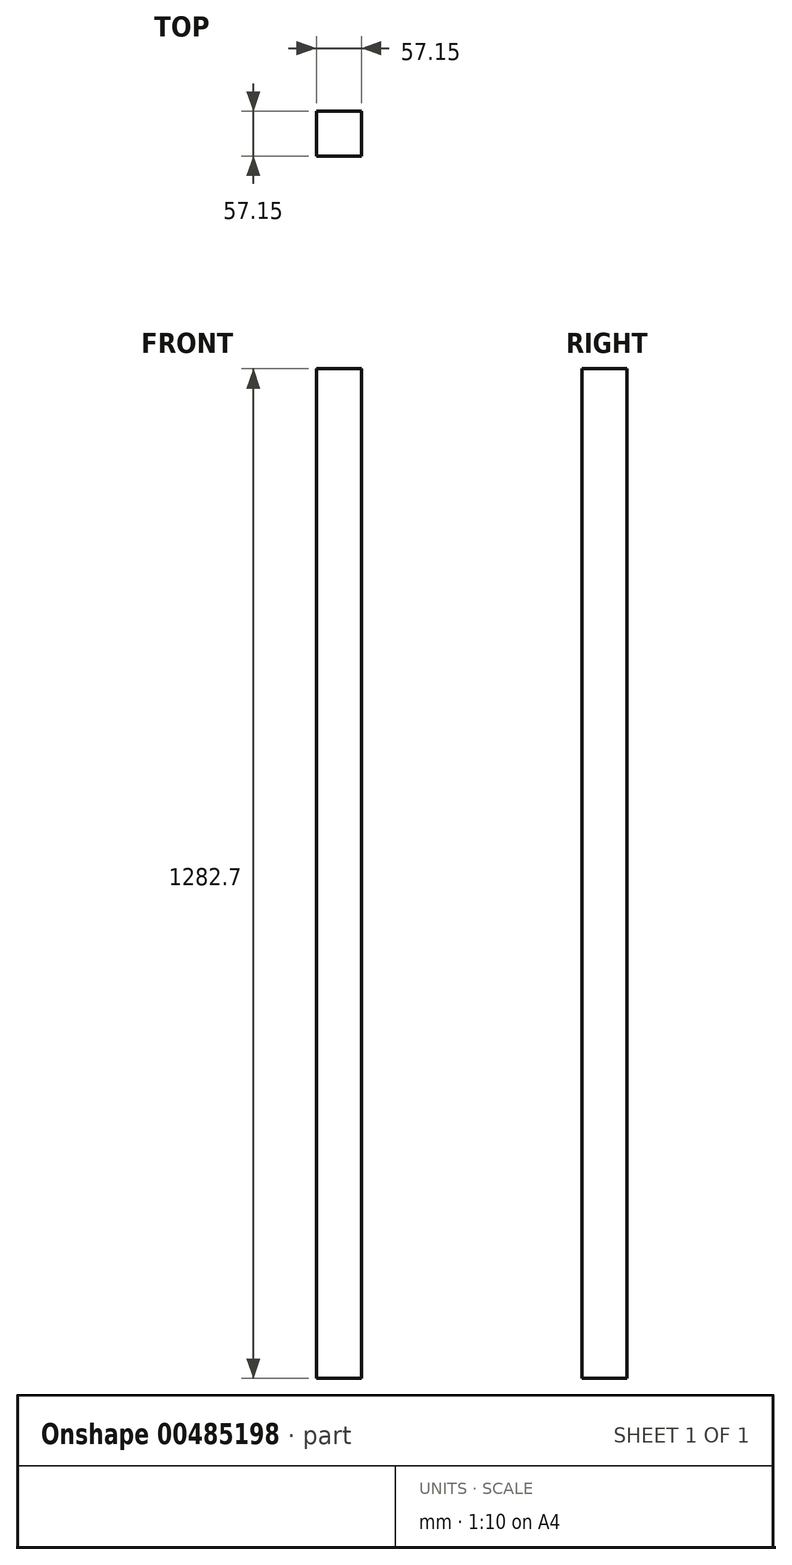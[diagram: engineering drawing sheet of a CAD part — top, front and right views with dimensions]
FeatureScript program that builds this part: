
annotation { "Feature Type Name" : "Feature", "Feature Type Description" : "" }
export const myFeature = defineFeature(function(context is Context, id is Id, definition is map)
    precondition{}
    {
        {
            var Q0;
            Q0=qCreatedBy(makeId("Front.planeOp"),FACE);
            var sketch = newSketch(context, id + "F0", { "sketchPlane" : qUnion([Q0])});
            skLineSegment(sketch, "E0.bottom", {"start": v(0, 0) * mm, "end": v(57.15, 0) * mm});
            skLineSegment(sketch, "E0.top", {"start": v(0, -1282.7) * mm, "end": v(57.15, -1282.7) * mm});
            skLineSegment(sketch, "E0.left", {"start": v(0, 0) * mm, "end": v(0, -1282.7) * mm});
            skLineSegment(sketch, "E0.right", {"start": v(57.15, 0) * mm, "end": v(57.15, -1282.7) * mm});
            skSolve(sketch);
        }
        {
            var Q0;
            Q0 = qSketchRegion(id + "F0", true);
            extrude(context, id + "F1", {"entities" : qUnion([Q0]), "oppositeDirection" : true, "depth" : 57.15 * mm});
        }
    });
